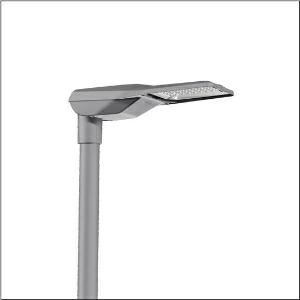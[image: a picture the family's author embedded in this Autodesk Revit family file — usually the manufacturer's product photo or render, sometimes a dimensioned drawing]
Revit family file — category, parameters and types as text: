
# Revit family: streetlight_sl_21_iq_mini___st0_8a_5xe2c31d08gb_9b37
name_source: partatom
category: Lighting Fixtures
units: mm (PartAtom-declared; Revit-internal decimal feet)

## family parameters
Cut with Voids When Loaded = No
Host = Face
Light Source = No
Part Type = Normal
Room Calculation Point = No
Round Connector Dimension = Use Diameter
Shared = No

## types (1)
- --- (1 x LED, 5680 lm, 37.1 W, 3000K)
    Apparent Load = 37 VA
    CIE Flux Codes = 38 75 97 100 100
    Color Rendering = 70
    Color Temperature = 3000K
    Default Elevation = 1800 mm
    Description = Streetlight SL 21 iQ mini, mast luminaire, primary light control with lens, of PMMA, primary optical cover: cover, of toughened safety glass, transparent, light distribution: ST0.8a, light emission: direct distribution, primary light characteristic: asymmetric, installation type: post-top, side-entry, LED, High Power LED, rated luminous flux: 5.680lm, luminous efficacy: 153lm/W, light colour: 730, colour temperature: 3000K, control: Auto-Match, Temp-Guard, Lumen-Switch, Night-Set, Smart-Wire, Light-Fading, Desk-Remote (wireless, voltage-free reading and setting of iQ features in the workshop via application-optimized NFC function/RFID function), optimised constant luminous flux control (CLO 2.0), presetting dimming linear, mains connection: 220..240V, AC, 50/60Hz, start of lifetime: 37W, end of service life: 39W, reduction: 18W, luminaire housing, of diecast aluminium, powder-coated, Siteco® metallic grey (DB 702S), corrosivity category C5 mid according to DIN EN ISO 12944, please order mast flange separately, inclination adjustable: 0°, 5°, 10°, 15°, sealing non-destructively replaceable, multi-level sealing system, length: 628mm, width: 235mm, height: 110mm, mast flange for spigot size: 42mm (side-entry): 5XC10008XM4, 60/48mm (side-entry/post-top): 5XC10108XM2, 76/60mm (side-entry/post-top): 5XC10108XM1, protection rating (complete): IP66, insulation class (complete): insulation class II (safety insulation), certification: CE, ENEC, ENEC+, VDE, impact resistance: IK09, permissible operating ambient temperature for outdoor applications: -40..+50°C, standard-compliant lighting for roads and squares, packaging unit: 1 piece

Light Distribution: ST0.8a
    Height = 110 mm
    Lamp = 1 x LED
    Lamp Light Flux = 5680 lm
    Lamp Power = 37.1 W
    Lamp count = 1
    Length = 625 mm
    Luminous efficacy = 153 lm/W
    Manufacturer = Siteco
    ModVariant = No
    Model = 5XE2C31D08GB
    Number of Poles = 1
    OnlyDefault = Yes
    Power Factor = 1
    Product Name = Streetlight SL 21 iQ mini | ST0.8a
    Product group = mast luminaire | pylon top
    ProductGroupID = 6100
    Protection Class = Protection class II
    Protection Degree = IP 66
    RLX_Detail_Level = 1
    RLX_Emergency_Light_Flux = 0 lm
    RLX_Emergency_Type = 0
    RLX_Emergency_Type_DB = No
    RlxData = <blob elided: 94281 chars, md5=fdb09366>
    Socket = socket
    Standby Power = 0 W
    System Light Flux = 5680 lm
    System Power = 37 W
    Type Comments = factory setting: luminous flux: 100 % | dim-lin: 254 | 385 mA
    Type Image = l_1003519.jpg
    URL = http://relux.com
    VarID = @adj_118987
    Voltage = 0 V
    Weight = 0.00 kg
    Width = 234 mm

## geometry (parser evidence)
native form markers: Blend x4, Sweep x11
no freeform markers — native parametric forms only
